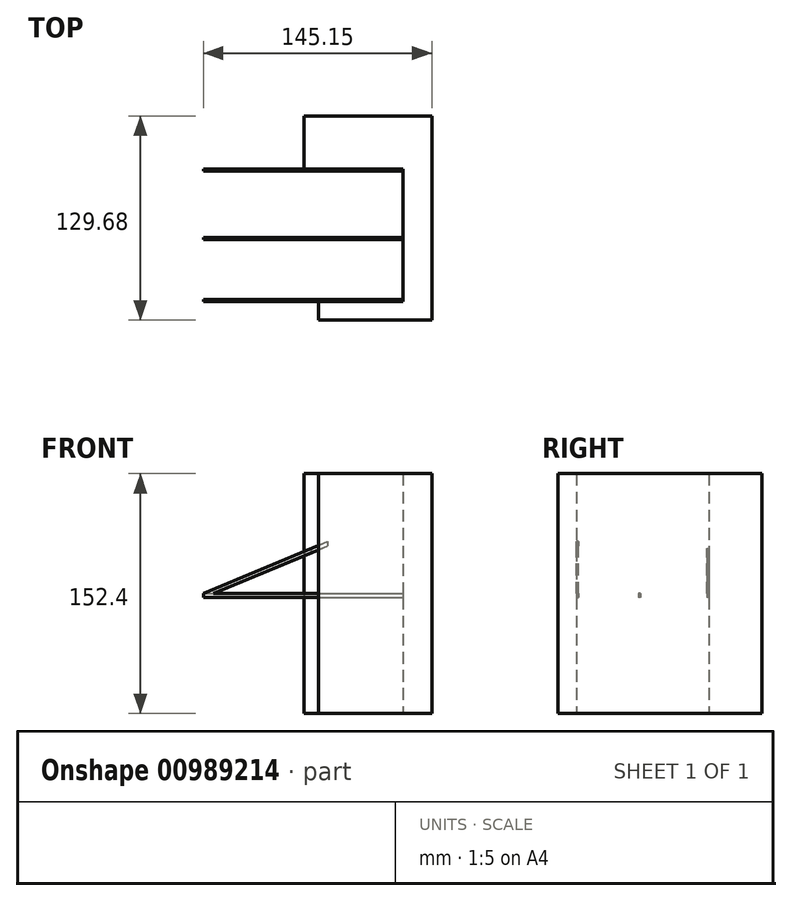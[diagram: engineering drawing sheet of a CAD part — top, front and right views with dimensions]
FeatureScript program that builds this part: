
annotation { "Feature Type Name" : "Feature", "Feature Type Description" : "" }
export const myFeature = defineFeature(function(context is Context, id is Id, definition is map)
    precondition{}
    {
        {
            var Q0;
            Q0=qCreatedBy(makeId("Top.planeOp"),FACE);
            var sketch = newSketch(context, id + "F0", { "sketchPlane" : qUnion([Q0])});
            skLineSegment(sketch, "E0.bottom", {"start": v(0, 0) * mm, "end": v(41.4, 0) * mm});
            skLineSegment(sketch, "E0.top", {"start": v(0, 0) * mm, "end": v(41.4, 0) * mm});
            skLineSegment(sketch, "E0.left", {"start": v(0, 0) * mm, "end": v(0, 0) * mm});
            skLineSegment(sketch, "E0.right", {"start": v(41.4, 0) * mm, "end": v(41.4, 0) * mm});
            skLineSegment(sketch, "E1.bottom", {"start": v(41.4, -84.33) * mm, "end": v(0, -84.33) * mm});
            skLineSegment(sketch, "E1.top", {"start": v(41.4, 0) * mm, "end": v(0, 0) * mm});
            skLineSegment(sketch, "E1.left", {"start": v(41.4, -84.33) * mm, "end": v(41.4, 0) * mm});
            skLineSegment(sketch, "E1.right", {"start": v(0, -84.33) * mm, "end": v(0, 0) * mm});
            skLineSegment(sketch, "E2", {"start": v(0, -84.33) * mm, "end": v(-9.14, -84.33) * mm});
            skLineSegment(sketch, "E3", {"start": v(-9.14, -84.33) * mm, "end": v(-9.14, 0) * mm});
            skLineSegment(sketch, "E4", {"start": v(-9.14, 0) * mm, "end": v(0, 0) * mm});
            skLineSegment(sketch, "E5.bottom", {"start": v(-9.14, -84.33) * mm, "end": v(-73.15, -84.33) * mm});
            skLineSegment(sketch, "E5.top", {"start": v(-9.14, 0) * mm, "end": v(-73.15, 0) * mm});
            skLineSegment(sketch, "E5.right", {"start": v(-73.15, -84.33) * mm, "end": v(-73.15, 0) * mm});
            skSolve(sketch);
        }
        {
            var Q0;
            Q0=qCreatedBy(makeId("Top.planeOp"),FACE);
            var sketch = newSketch(context, id + "F1", { "sketchPlane" : qUnion([Q0])});
            skLineSegment(sketch, "E6.bottom", {"start": v(53.51, 0) * mm, "end": v(-9.14, 0) * mm});
            skLineSegment(sketch, "E6.top", {"start": v(53.51, 33.66) * mm, "end": v(-9.14, 33.66) * mm});
            skLineSegment(sketch, "E6.right", {"start": v(-9.14, 0) * mm, "end": v(-9.14, 33.66) * mm});
            skLineSegment(sketch, "E7.bottom", {"start": v(53.51, 33.66) * mm, "end": v(72, 33.66) * mm});
            skLineSegment(sketch, "E7.top", {"start": v(53.51, -96.02) * mm, "end": v(72, -96.02) * mm});
            skLineSegment(sketch, "E7.left", {"start": v(53.51, 0) * mm, "end": v(53.51, -84.33) * mm});
            skLineSegment(sketch, "E7.right", {"start": v(72, 33.66) * mm, "end": v(72, -96.02) * mm});
            skLineSegment(sketch, "E8.bottom", {"start": v(53.51, -96.02) * mm, "end": v(0, -96.02) * mm});
            skLineSegment(sketch, "E8.top", {"start": v(53.51, -84.33) * mm, "end": v(0, -84.33) * mm});
            skLineSegment(sketch, "E8.right", {"start": v(0, -96.02) * mm, "end": v(0, -84.33) * mm});
            skSolve(sketch);
        }
        {
            var Q0;
            Q0 = qSketchRegion(id + "F1", true);
            extrude(context, id + "F2", {"entities" : qUnion([Q0]), "depth" : 152.4 * mm, "offsetDistance" : 25.4 * mm});
        }
        {
            var Q0;
            Q0=makeQuery(id+"F2.opExtrude","SWEPT_FACE",FACE,{"disambiguationData":[OSD([sQuery(id+"F1.wireOp",EDGE,"E7.left")])]});
            var sketch = newSketch(context, id + "F3", { "sketchPlane" : qUnion([Q0])});
            skLineSegment(sketch, "E9.bottom", {"start": v(0, 76.2) * mm, "end": v(1.27, 76.2) * mm});
            skLineSegment(sketch, "E9.top", {"start": v(0, 73.66) * mm, "end": v(1.27, 73.66) * mm});
            skLineSegment(sketch, "E9.left", {"start": v(0, 76.2) * mm, "end": v(0, 73.66) * mm});
            skLineSegment(sketch, "E9.right", {"start": v(1.27, 76.2) * mm, "end": v(1.27, 73.66) * mm});
            skLineSegment(sketch, "E10.bottom", {"start": v(84.33, 76.2) * mm, "end": v(83.06, 76.2) * mm});
            skLineSegment(sketch, "E10.top", {"start": v(84.33, 73.66) * mm, "end": v(83.06, 73.66) * mm});
            skLineSegment(sketch, "E10.left", {"start": v(84.33, 76.2) * mm, "end": v(84.33, 73.66) * mm});
            skLineSegment(sketch, "E10.right", {"start": v(83.06, 76.2) * mm, "end": v(83.06, 73.66) * mm});
            skLineSegment(sketch, "E11.bottom", {"start": v(43.52, 76.2) * mm, "end": v(44.8, 76.2) * mm});
            skLineSegment(sketch, "E11.top", {"start": v(43.52, 73.66) * mm, "end": v(44.8, 73.66) * mm});
            skLineSegment(sketch, "E11.left", {"start": v(43.52, 76.2) * mm, "end": v(43.52, 73.66) * mm});
            skLineSegment(sketch, "E11.right", {"start": v(44.8, 76.2) * mm, "end": v(44.8, 73.66) * mm});
            skSolve(sketch);
        }
        {
            var Q0;
            Q0 = qSketchRegion(id + "F3", true);
            var Q1;
            Q1=sQuery(id+"F0.wireOp",VERTEX,"E5.top.end");
            extrude(context, id + "F4", {"entities" : qUnion([Q0]), "operationType" : NewBodyOperationType.ADD, "endBound" : BoundingType.UP_TO_VERTEX, "depth" : 25.4 * mm, "endBoundEntityVertex" : qUnion([Q1]), "offsetDistance" : 25.4 * mm});
        }
        {
            var Q0;
            Q0=makeQuery(id+"F4.opExtrude","SWEPT_FACE",FACE,{"disambiguationData":[OSD([sQuery(id+"F3.wireOp",EDGE,"E9.right")])]});
            var sketch = newSketch(context, id + "F5", { "sketchPlane" : qUnion([Q0])});
            skLineSegment(sketch, "E12.bottom", {"start": v(-73.15, 76.2) * mm, "end": v(-71.88, 76.2) * mm});
            skLineSegment(sketch, "E12.top", {"start": v(-73.15, 73.66) * mm, "end": v(-71.88, 73.66) * mm});
            skLineSegment(sketch, "E12.left", {"start": v(-73.15, 76.2) * mm, "end": v(-73.15, 73.66) * mm});
            skLineSegment(sketch, "E12.right", {"start": v(-71.88, 76.2) * mm, "end": v(-71.88, 73.66) * mm});
            skLineSegment(sketch, "E13.1.0.0", {"start": v(-63, 76.2) * mm, "end": v(-61.72, 76.2) * mm});
            skLineSegment(sketch, "E13.1.0.1", {"start": v(-63, 76.2) * mm, "end": v(-63, 73.66) * mm});
            skLineSegment(sketch, "E13.1.0.2", {"start": v(-63, 73.66) * mm, "end": v(-61.72, 73.66) * mm});
            skLineSegment(sketch, "E13.1.0.3", {"start": v(-61.72, 76.2) * mm, "end": v(-61.72, 73.66) * mm});
            skLineSegment(sketch, "E13.2.0.0", {"start": v(-52.83, 76.2) * mm, "end": v(-51.56, 76.2) * mm});
            skLineSegment(sketch, "E13.2.0.1", {"start": v(-52.83, 76.2) * mm, "end": v(-52.83, 73.66) * mm});
            skLineSegment(sketch, "E13.2.0.2", {"start": v(-52.83, 73.66) * mm, "end": v(-51.56, 73.66) * mm});
            skLineSegment(sketch, "E13.2.0.3", {"start": v(-51.56, 76.2) * mm, "end": v(-51.56, 73.66) * mm});
            skLineSegment(sketch, "E13.3.0.0", {"start": v(-42.67, 76.2) * mm, "end": v(-41.4, 76.2) * mm});
            skLineSegment(sketch, "E13.3.0.1", {"start": v(-42.67, 76.2) * mm, "end": v(-42.67, 73.66) * mm});
            skLineSegment(sketch, "E13.3.0.2", {"start": v(-42.67, 73.66) * mm, "end": v(-41.4, 73.66) * mm});
            skLineSegment(sketch, "E13.3.0.3", {"start": v(-41.4, 76.2) * mm, "end": v(-41.4, 73.66) * mm});
            skLineSegment(sketch, "E13.4.0.0", {"start": v(-32.51, 76.2) * mm, "end": v(-31.24, 76.2) * mm});
            skLineSegment(sketch, "E13.4.0.1", {"start": v(-32.51, 76.2) * mm, "end": v(-32.51, 73.66) * mm});
            skLineSegment(sketch, "E13.4.0.2", {"start": v(-32.51, 73.66) * mm, "end": v(-31.24, 73.66) * mm});
            skLineSegment(sketch, "E13.4.0.3", {"start": v(-31.24, 76.2) * mm, "end": v(-31.24, 73.66) * mm});
            skLineSegment(sketch, "E13.5.0.0", {"start": v(-22.35, 76.2) * mm, "end": v(-21.08, 76.2) * mm});
            skLineSegment(sketch, "E13.5.0.1", {"start": v(-22.35, 76.2) * mm, "end": v(-22.35, 73.66) * mm});
            skLineSegment(sketch, "E13.5.0.2", {"start": v(-22.35, 73.66) * mm, "end": v(-21.08, 73.66) * mm});
            skLineSegment(sketch, "E13.5.0.3", {"start": v(-21.08, 76.2) * mm, "end": v(-21.08, 73.66) * mm});
            skLineSegment(sketch, "E13.6.0.0", {"start": v(-12.2, 76.2) * mm, "end": v(-10.92, 76.2) * mm});
            skLineSegment(sketch, "E13.6.0.1", {"start": v(-12.2, 76.2) * mm, "end": v(-12.2, 73.66) * mm});
            skLineSegment(sketch, "E13.6.0.2", {"start": v(-12.2, 73.66) * mm, "end": v(-10.92, 73.66) * mm});
            skLineSegment(sketch, "E13.6.0.3", {"start": v(-10.92, 76.2) * mm, "end": v(-10.92, 73.66) * mm});
            skLineSegment(sketch, "E13.direction1", {"start": v(-73.15, 73.66) * mm, "end": v(-63, 73.66) * mm, "construction": true});
            skLineSegment(sketch, "E14.0.7.0", {"start": v(-2.03, 76.2) * mm, "end": v(-0.76, 76.2) * mm});
            skLineSegment(sketch, "E14.3.7.0", {"start": v(-2.03, 76.2) * mm, "end": v(-2.03, 73.66) * mm});
            skLineSegment(sketch, "E14.6.7.0", {"start": v(-2.03, 73.66) * mm, "end": v(-0.76, 73.66) * mm});
            skLineSegment(sketch, "E14.9.7.0", {"start": v(-0.76, 76.2) * mm, "end": v(-0.76, 73.66) * mm});
            skLineSegment(sketch, "E14.0.8.0", {"start": v(8.13, 76.2) * mm, "end": v(9.4, 76.2) * mm});
            skLineSegment(sketch, "E14.3.8.0", {"start": v(8.13, 76.2) * mm, "end": v(8.13, 73.66) * mm});
            skLineSegment(sketch, "E14.6.8.0", {"start": v(8.13, 73.66) * mm, "end": v(9.4, 73.66) * mm});
            skLineSegment(sketch, "E14.9.8.0", {"start": v(9.4, 76.2) * mm, "end": v(9.4, 73.66) * mm});
            skLineSegment(sketch, "E14.0.9.0", {"start": v(18.29, 76.2) * mm, "end": v(19.56, 76.2) * mm});
            skLineSegment(sketch, "E14.3.9.0", {"start": v(18.29, 76.2) * mm, "end": v(18.29, 73.66) * mm});
            skLineSegment(sketch, "E14.6.9.0", {"start": v(18.29, 73.66) * mm, "end": v(19.56, 73.66) * mm});
            skLineSegment(sketch, "E14.9.9.0", {"start": v(19.56, 76.2) * mm, "end": v(19.56, 73.66) * mm});
            skLineSegment(sketch, "E14.0.10.0", {"start": v(28.45, 76.2) * mm, "end": v(29.72, 76.2) * mm});
            skLineSegment(sketch, "E14.3.10.0", {"start": v(28.45, 76.2) * mm, "end": v(28.45, 73.66) * mm});
            skLineSegment(sketch, "E14.6.10.0", {"start": v(28.45, 73.66) * mm, "end": v(29.72, 73.66) * mm});
            skLineSegment(sketch, "E14.9.10.0", {"start": v(29.72, 76.2) * mm, "end": v(29.72, 73.66) * mm});
            skLineSegment(sketch, "E14.0.11.0", {"start": v(38.6, 76.2) * mm, "end": v(39.88, 76.2) * mm});
            skLineSegment(sketch, "E14.3.11.0", {"start": v(38.6, 76.2) * mm, "end": v(38.6, 73.66) * mm});
            skLineSegment(sketch, "E14.6.11.0", {"start": v(38.6, 73.66) * mm, "end": v(39.88, 73.66) * mm});
            skLineSegment(sketch, "E14.9.11.0", {"start": v(39.88, 76.2) * mm, "end": v(39.88, 73.66) * mm});
            skSolve(sketch);
        }
        {
            var Q0;
            Q0 = qConstructionFilter(qBodyType(qCreatedBy(id + "F5" ,EDGE), BodyType.WIRE), ConstructionObject.NO);
            extrude(context, id + "F6", {"bodyType" : ToolBodyType.SURFACE, "surfaceEntities" : qUnion([Q0]), "endBound" : BoundingType.UP_TO_NEXT, "depth" : 25.4 * mm, "offsetDistance" : 25.4 * mm});
        }
        {
            var Q0;
            {var subQ2=sQuery(id+"F1.wireOp",EDGE,"E6.bottom");Q0=makeQuery(id+"F4.boolean.opBoolean","SPLIT",FACE,{"disambiguationData":[TD([makeQuery(id+"F4.opExtrude","SWEPT_FACE",FACE,{"disambiguationData":[OSD([sQuery(id+"F3.wireOp",EDGE,"E9.bottom")])]})])],"derivedFrom":makeQuery(id+"F2.opExtrude","SWEPT_FACE",FACE,{"disambiguationData":[OSD([subQ2])]})});}
            var sketch = newSketch(context, id + "F7", { "sketchPlane" : qUnion([Q0])});
            skLineSegment(sketch, "E15", {"start": v(-73.15, 76.2) * mm, "end": v(-4.74, 104.82) * mm});
            skLineSegment(sketch, "E16", {"start": v(-4.74, 104.82) * mm, "end": v(-4.74, 102.07) * mm});
            skLineSegment(sketch, "E17", {"start": v(-4.74, 102.07) * mm, "end": v(-66.57, 76.2) * mm});
            skLineSegment(sketch, "E18", {"start": v(-66.57, 76.2) * mm, "end": v(-73.15, 76.2) * mm});
            skSolve(sketch);
        }
        {
            var Q0;
            Q0 = qSketchRegion(id + "F7", true);
            extrude(context, id + "F8", {"entities" : qUnion([Q0]), "operationType" : NewBodyOperationType.ADD, "depth" : 1.27 * mm, "offsetDistance" : 25.4 * mm});
        }
        {
            var Q0;
            Q0=makeQuery(id+"F4.opExtrude","SWEPT_FACE",FACE,{"disambiguationData":[OSD([sQuery(id+"F3.wireOp",EDGE,"E11.right")])]});
            var sketch = newSketch(context, id + "F9", { "sketchPlane" : qUnion([Q0])});
            skLineSegment(sketch, "E19.bottom", {"start": v(-73.15, 76.2) * mm, "end": v(-71.88, 76.2) * mm});
            skLineSegment(sketch, "E19.top", {"start": v(-73.15, 73.66) * mm, "end": v(-71.88, 73.66) * mm});
            skLineSegment(sketch, "E19.left", {"start": v(-73.15, 76.2) * mm, "end": v(-73.15, 73.66) * mm});
            skLineSegment(sketch, "E19.right", {"start": v(-71.88, 76.2) * mm, "end": v(-71.88, 73.66) * mm});
            skLineSegment(sketch, "E20.1.0.0", {"start": v(-63, 76.2) * mm, "end": v(-61.72, 76.2) * mm});
            skLineSegment(sketch, "E20.1.0.1", {"start": v(-63, 76.2) * mm, "end": v(-63, 73.66) * mm});
            skLineSegment(sketch, "E20.1.0.2", {"start": v(-63, 73.66) * mm, "end": v(-61.72, 73.66) * mm});
            skLineSegment(sketch, "E20.1.0.3", {"start": v(-61.72, 76.2) * mm, "end": v(-61.72, 73.66) * mm});
            skLineSegment(sketch, "E20.2.0.0", {"start": v(-52.83, 76.2) * mm, "end": v(-51.56, 76.2) * mm});
            skLineSegment(sketch, "E20.2.0.1", {"start": v(-52.83, 76.2) * mm, "end": v(-52.83, 73.66) * mm});
            skLineSegment(sketch, "E20.2.0.2", {"start": v(-52.83, 73.66) * mm, "end": v(-51.56, 73.66) * mm});
            skLineSegment(sketch, "E20.2.0.3", {"start": v(-51.56, 76.2) * mm, "end": v(-51.56, 73.66) * mm});
            skLineSegment(sketch, "E20.3.0.0", {"start": v(-42.67, 76.2) * mm, "end": v(-41.4, 76.2) * mm});
            skLineSegment(sketch, "E20.3.0.1", {"start": v(-42.67, 76.2) * mm, "end": v(-42.67, 73.66) * mm});
            skLineSegment(sketch, "E20.3.0.2", {"start": v(-42.67, 73.66) * mm, "end": v(-41.4, 73.66) * mm});
            skLineSegment(sketch, "E20.3.0.3", {"start": v(-41.4, 76.2) * mm, "end": v(-41.4, 73.66) * mm});
            skLineSegment(sketch, "E20.4.0.0", {"start": v(-32.51, 76.2) * mm, "end": v(-31.24, 76.2) * mm});
            skLineSegment(sketch, "E20.4.0.1", {"start": v(-32.51, 76.2) * mm, "end": v(-32.51, 73.66) * mm});
            skLineSegment(sketch, "E20.4.0.2", {"start": v(-32.51, 73.66) * mm, "end": v(-31.24, 73.66) * mm});
            skLineSegment(sketch, "E20.4.0.3", {"start": v(-31.24, 76.2) * mm, "end": v(-31.24, 73.66) * mm});
            skLineSegment(sketch, "E20.5.0.0", {"start": v(-22.35, 76.2) * mm, "end": v(-21.08, 76.2) * mm});
            skLineSegment(sketch, "E20.5.0.1", {"start": v(-22.35, 76.2) * mm, "end": v(-22.35, 73.66) * mm});
            skLineSegment(sketch, "E20.5.0.2", {"start": v(-22.35, 73.66) * mm, "end": v(-21.08, 73.66) * mm});
            skLineSegment(sketch, "E20.5.0.3", {"start": v(-21.08, 76.2) * mm, "end": v(-21.08, 73.66) * mm});
            skLineSegment(sketch, "E20.6.0.0", {"start": v(-12.2, 76.2) * mm, "end": v(-10.92, 76.2) * mm});
            skLineSegment(sketch, "E20.6.0.1", {"start": v(-12.2, 76.2) * mm, "end": v(-12.2, 73.66) * mm});
            skLineSegment(sketch, "E20.6.0.2", {"start": v(-12.2, 73.66) * mm, "end": v(-10.92, 73.66) * mm});
            skLineSegment(sketch, "E20.6.0.3", {"start": v(-10.92, 76.2) * mm, "end": v(-10.92, 73.66) * mm});
            skLineSegment(sketch, "E20.direction1", {"start": v(-73.15, 73.66) * mm, "end": v(-63, 73.66) * mm, "construction": true});
            skLineSegment(sketch, "E21.0.7.0", {"start": v(-2.03, 76.2) * mm, "end": v(-0.76, 76.2) * mm});
            skLineSegment(sketch, "E21.3.7.0", {"start": v(-2.03, 76.2) * mm, "end": v(-2.03, 73.66) * mm});
            skLineSegment(sketch, "E21.6.7.0", {"start": v(-2.03, 73.66) * mm, "end": v(-0.76, 73.66) * mm});
            skLineSegment(sketch, "E21.9.7.0", {"start": v(-0.76, 76.2) * mm, "end": v(-0.76, 73.66) * mm});
            skLineSegment(sketch, "E21.0.8.0", {"start": v(8.13, 76.2) * mm, "end": v(9.4, 76.2) * mm});
            skLineSegment(sketch, "E21.3.8.0", {"start": v(8.13, 76.2) * mm, "end": v(8.13, 73.66) * mm});
            skLineSegment(sketch, "E21.6.8.0", {"start": v(8.13, 73.66) * mm, "end": v(9.4, 73.66) * mm});
            skLineSegment(sketch, "E21.9.8.0", {"start": v(9.4, 76.2) * mm, "end": v(9.4, 73.66) * mm});
            skLineSegment(sketch, "E21.0.9.0", {"start": v(18.29, 76.2) * mm, "end": v(19.56, 76.2) * mm});
            skLineSegment(sketch, "E21.3.9.0", {"start": v(18.29, 76.2) * mm, "end": v(18.29, 73.66) * mm});
            skLineSegment(sketch, "E21.6.9.0", {"start": v(18.29, 73.66) * mm, "end": v(19.56, 73.66) * mm});
            skLineSegment(sketch, "E21.9.9.0", {"start": v(19.56, 76.2) * mm, "end": v(19.56, 73.66) * mm});
            skLineSegment(sketch, "E21.0.10.0", {"start": v(28.45, 76.2) * mm, "end": v(29.72, 76.2) * mm});
            skLineSegment(sketch, "E21.3.10.0", {"start": v(28.45, 76.2) * mm, "end": v(28.45, 73.66) * mm});
            skLineSegment(sketch, "E21.6.10.0", {"start": v(28.45, 73.66) * mm, "end": v(29.72, 73.66) * mm});
            skLineSegment(sketch, "E21.9.10.0", {"start": v(29.72, 76.2) * mm, "end": v(29.72, 73.66) * mm});
            skLineSegment(sketch, "E21.0.11.0", {"start": v(38.6, 76.2) * mm, "end": v(39.88, 76.2) * mm});
            skLineSegment(sketch, "E21.3.11.0", {"start": v(38.6, 76.2) * mm, "end": v(38.6, 73.66) * mm});
            skLineSegment(sketch, "E21.6.11.0", {"start": v(38.6, 73.66) * mm, "end": v(39.88, 73.66) * mm});
            skLineSegment(sketch, "E21.9.11.0", {"start": v(39.88, 76.2) * mm, "end": v(39.88, 73.66) * mm});
            skSolve(sketch);
        }
        {
            var Q0;
            Q0 = qConstructionFilter(qBodyType(qCreatedBy(id + "F9" ,EDGE), BodyType.WIRE), ConstructionObject.NO);
            var Q1;
            Q1=makeQuery(id+"F4.opExtrude","SWEPT_FACE",FACE,{"disambiguationData":[OSD([sQuery(id+"F3.wireOp",EDGE,"E10.right")])]});
            extrude(context, id + "F10", {"bodyType" : ToolBodyType.SURFACE, "surfaceEntities" : qUnion([Q0]), "endBound" : BoundingType.UP_TO_SURFACE, "depth" : 25.4 * mm, "endBoundEntityFace" : qUnion([Q1]), "offsetDistance" : 25.4 * mm});
        }
        {
            var Q0;
            {var subQ2=sQuery(id+"F1.wireOp",EDGE,"E8.top");Q0=makeQuery(id+"F4.boolean.opBoolean","SPLIT",FACE,{"disambiguationData":[TD([makeQuery(id+"F4.opExtrude","SWEPT_FACE",FACE,{"disambiguationData":[OSD([sQuery(id+"F3.wireOp",EDGE,"E10.bottom")])]})])],"derivedFrom":makeQuery(id+"F2.opExtrude","SWEPT_FACE",FACE,{"disambiguationData":[OSD([subQ2])]})});}
            var sketch = newSketch(context, id + "F11", { "sketchPlane" : qUnion([Q0])});
            skLineSegment(sketch, "E22.1", {"start": v(9.14, 100.22) * mm, "end": v(66.57, 76.2) * mm});
            skLineSegment(sketch, "E22.2", {"start": v(73.15, 76.2) * mm, "end": v(9.14, 102.97) * mm});
            skLineSegment(sketch, "E23", {"start": v(66.57, 76.2) * mm, "end": v(73.15, 76.2) * mm});
            skLineSegment(sketch, "E24", {"start": v(9.14, 102.97) * mm, "end": v(-5.76, 109.21) * mm});
            skLineSegment(sketch, "E25", {"start": v(9.14, 100.22) * mm, "end": v(-5.76, 106.46) * mm});
            skLineSegment(sketch, "E26", {"start": v(-5.76, 109.21) * mm, "end": v(-5.76, 106.46) * mm});
            skSolve(sketch);
        }
        {
            var Q0;
            Q0 = qSketchRegion(id + "F11", true);
            extrude(context, id + "F12", {"entities" : qUnion([Q0]), "operationType" : NewBodyOperationType.ADD, "depth" : 1.27 * mm, "offsetDistance" : 25.4 * mm});
        }
    });
